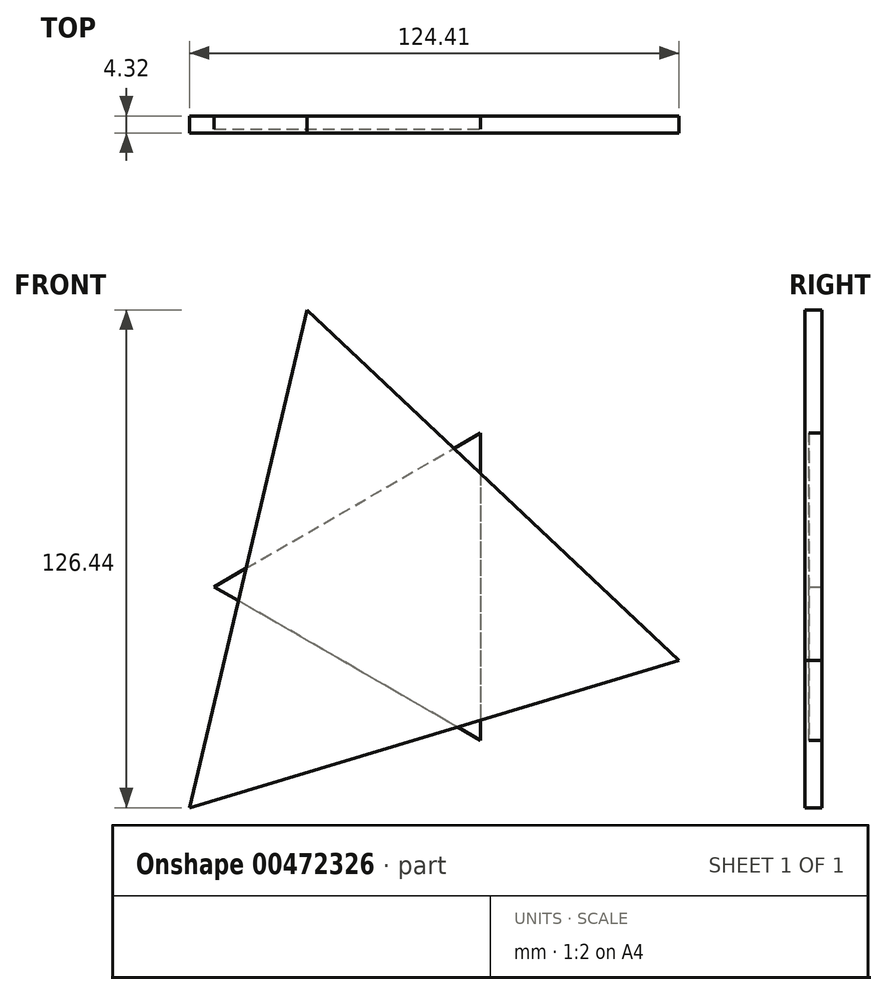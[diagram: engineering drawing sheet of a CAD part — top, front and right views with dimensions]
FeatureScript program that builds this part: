
annotation { "Feature Type Name" : "Feature", "Feature Type Description" : "" }
export const myFeature = defineFeature(function(context is Context, id is Id, definition is map)
    precondition{}
    {
        {
            var Q0;
            Q0=qCreatedBy(makeId("Front.planeOp"),FACE);
            var sketch = newSketch(context, id + "F0", { "sketchPlane" : qUnion([Q0])});
            skCircle(sketch, "E0.cCircle", {"center": v(0, 0) * mm, "radius": 37.5 * mm, "construction": true});
            skLineSegment(sketch, "E0.0", {"start": v(73, -17.22) * mm, "end": v(-51.41, -54.61) * mm});
            skLineSegment(sketch, "E0.1", {"start": v(-51.41, -54.61) * mm, "end": v(-21.59, 71.83) * mm});
            skLineSegment(sketch, "E0.2", {"start": v(-21.59, 71.83) * mm, "end": v(73, -17.22) * mm});
            skPoint(sketch, "E0.0.midPoint", {"position": v(10.8, -35.92) * mm});
            skSolve(sketch);
        }
        {
            var Q0;
            Q0 = qSketchRegion(id + "F0", true);
            extrude(context, id + "F1", {"entities" : qUnion([Q0]), "depth" : 4.32 * mm, "offsetDistance" : 25.4 * mm});
        }
        {
            var Q0;
            Q0=qCreatedBy(makeId("Front.planeOp"),FACE);
            var sketch = newSketch(context, id + "F2", { "sketchPlane" : qUnion([Q0])});
            skCircle(sketch, "E1.cCircle", {"center": v(0, 1.5) * mm, "radius": 22.55 * mm, "construction": true});
            skLineSegment(sketch, "E1.0", {"start": v(22.55, 40.57) * mm, "end": v(22.55, -37.55) * mm});
            skLineSegment(sketch, "E1.1", {"start": v(22.55, -37.55) * mm, "end": v(-45.1, 1.5) * mm});
            skLineSegment(sketch, "E1.2", {"start": v(-45.1, 1.5) * mm, "end": v(22.55, 40.57) * mm});
            skPoint(sketch, "E1.0.midPoint", {"position": v(22.55, 1.5) * mm});
            skSolve(sketch);
        }
        {
            var Q0;
            Q0 = qSketchRegion(id + "F2", true);
            extrude(context, id + "F3", {"entities" : qUnion([Q0]), "depth" : 3.3 * mm, "offsetDistance" : 25.4 * mm});
        }
    });
